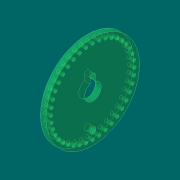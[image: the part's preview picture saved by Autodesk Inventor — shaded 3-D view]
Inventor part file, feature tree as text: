
AUTODESK INVENTOR PART (.ipt)
format: ipt  version: 2016 (Build 200138000, 138)  size: 193,024 bytes
history: native  units: mm
features: sketch x5, hole x3, extrude x2, projected_geometry x2, pattern_circular x1
ambient origin geometry x8: Origin, YZ Plane, XZ Plane, XY Plane, X Axis, Y Axis, Z Axis, Center Point
bodies: Solid1 (feature_tree)
feature tree (13):
  extrude  "Extrusion1"  Depth=5.588mm
  hole  "Hole1"  [1 undecoded]
  pattern_circular  "Circular Pattern1"  Count=40  [1 undecoded]
  hole  "Hole2"  [1 undecoded]
  extrude  "Extrusion2"  Depth=8.0mm
  hole  "Hole3"  [1 undecoded]
  sketch  "Sketch2"  dims[d7=90.0mm d8=5.588mm]
  sketch  "Sketch3"  dims[d9=0.0mm d10=40.325mm]
  projected_geometry  "Projected Loop1"
  sketch  "Sketch4"  dims[d11=3.1mm]
  sketch  "Sketch5"  dims[d12=6.0mm d13=4.0mm d14=2.0mm d15=90.0deg d16=8.0mm d17=20.594885mm d18=400.0mm]
  sketch  "Sketch6"  dims[d19=360.0deg d21=16.0mm d22=6.0mm d23=4.0mm d24=2.0mm d25=90.0deg d26=8.0mm d27=20.594885mm d28=5.0mm d29=13.0mm d30=10.0mm d31=0.0mm d32=8.0mm d33=0.0mm d34=6.0mm d35=6.0mm d36=4.0mm d37=2.0mm d38=90.0deg d39=8.0mm d40=20.594885mm]
  projected_geometry  "Projected Loop2"
note: 4 required parameter values undecoded (feature->parameter linkage not recoverable at this tier; creation-order binding heuristic only, values carry confidence <= 0.55)
